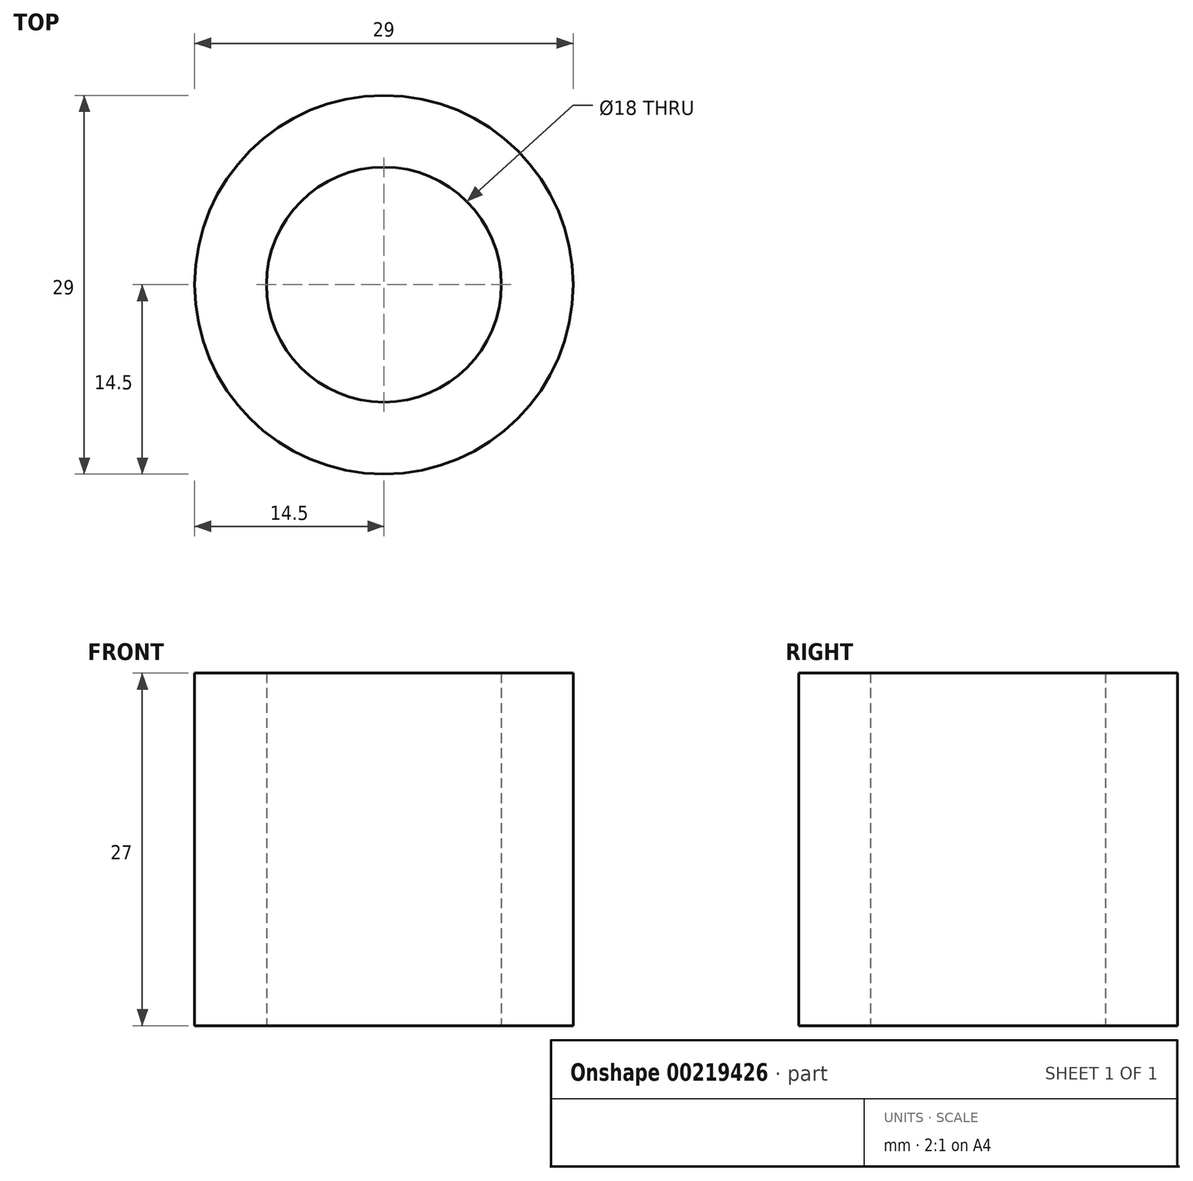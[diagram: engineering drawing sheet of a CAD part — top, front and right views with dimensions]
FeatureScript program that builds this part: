
annotation { "Feature Type Name" : "Feature", "Feature Type Description" : "" }
export const myFeature = defineFeature(function(context is Context, id is Id, definition is map)
    precondition{}
    {
        {
            var Q0;
            Q0=qCreatedBy(makeId("Top.planeOp"),FACE);
            var sketch = newSketch(context, id + "F0", { "sketchPlane" : qUnion([Q0])});
            skCircle(sketch, "E0", {"center": v(0, 0) * mm, "radius": 14.5 * mm});
            skCircle(sketch, "E1", {"center": v(0, 0) * mm, "radius": 9 * mm});
            skSolve(sketch);
        }
        {
            var Q0;
            Q0=makeQuery(id+"F0.imprint","IMPRINT",FACE,{"disambiguationData":[TD([[makeQuery(id+"F0.imprint","IMPRINT",EDGE,{"derivedFrom":sQuery(id+"F0.wireOp",EDGE,"E0")}),1.0]])]});
            extrude(context, id + "F1", {"entities" : qUnion([Q0]), "depth" : 27 * mm});
        }
    });
